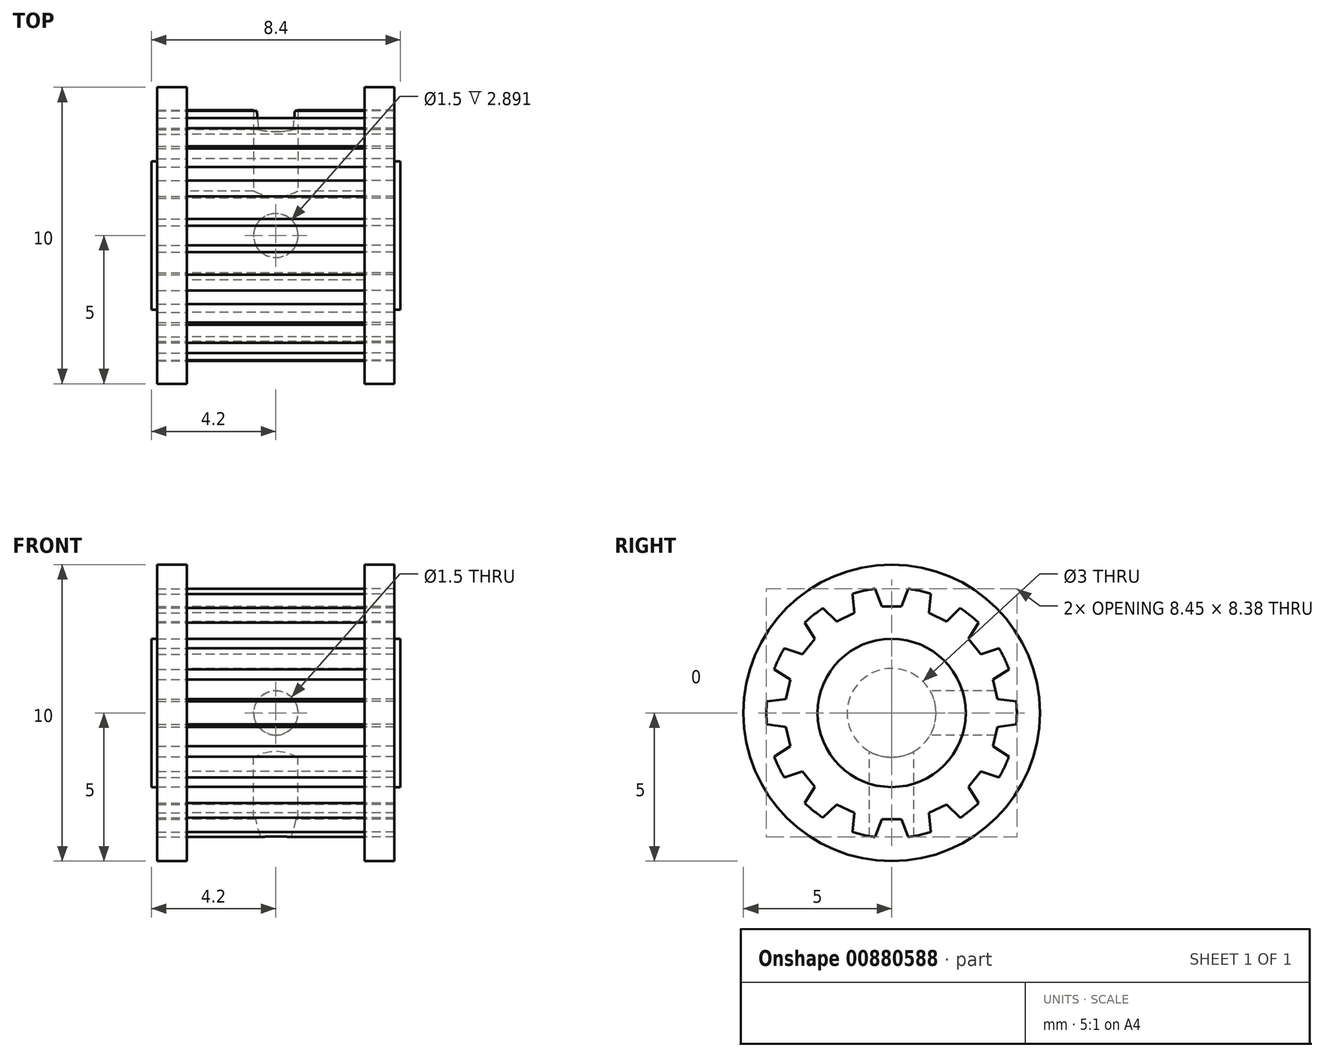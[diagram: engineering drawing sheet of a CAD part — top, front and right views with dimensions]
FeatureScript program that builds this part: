
annotation { "Feature Type Name" : "Feature", "Feature Type Description" : "" }
export const myFeature = defineFeature(function(context is Context, id is Id, definition is map)
    precondition{}
    {
        {
            var Q0;
            Q0=qCreatedBy(makeId("Right.planeOp"),FACE);
            var sketch = newSketch(context, id + "F0", { "sketchPlane" : qUnion([Q0])});
            skCircle(sketch, "E0", {"center": v(0, 0) * mm, "radius": 4.23 * mm});
            skSolve(sketch);
        }
        {
            var Q0;
            Q0=makeQuery(id+"F0.imprint","IMPRINT",FACE,{"disambiguationData":[TD([[makeQuery(id+"F0.imprint","IMPRINT",EDGE,{"derivedFrom":sQuery(id+"F0.wireOp",EDGE,"E0")}),1.0]])]});
            extrude(context, id + "F1", {"entities" : qUnion([Q0]), "endBound" : BoundingType.SYMMETRIC, "depth" : 6 * mm, "offsetDistance" : 25 * mm});
        }
        {
            var Q0;
            Q0=makeQuery(id+"F1.opExtrude","CAP_FACE",FACE,{"disambiguationData":[OSD([sQuery(id+"F0.wireOp",EDGE,"E0")])],"isStart":true});
            var sketch = newSketch(context, id + "F2", { "sketchPlane" : qUnion([Q0])});
            skCircle(sketch, "E1", {"center": v(0, 0) * mm, "radius": 1.5 * mm});
            skSolve(sketch);
        }
        {
            var Q0;
            Q0=makeQuery(id+"F2.imprint","IMPRINT",FACE,{"disambiguationData":[TD([[makeQuery(id+"F2.imprint","IMPRINT",EDGE,{"derivedFrom":sQuery(id+"F2.wireOp",EDGE,"E1")}),1.0]])]});
            extrude(context, id + "F3", {"entities" : qUnion([Q0]), "operationType" : NewBodyOperationType.REMOVE, "oppositeDirection" : true, "depth" : 6 * mm, "offsetDistance" : 25 * mm});
        }
        {
            var Q0;
            Q0=qCreatedBy(makeId("Front.planeOp"),FACE);
            var sketch = newSketch(context, id + "F4", { "sketchPlane" : qUnion([Q0])});
            skCircle(sketch, "E2", {"center": v(0, 0) * mm, "radius": 0.75 * mm});
            skSolve(sketch);
        }
        {
            var Q0;
            Q0=makeQuery(id+"F1.opExtrude","CAP_FACE",FACE,{"disambiguationData":[OSD([sQuery(id+"F0.wireOp",EDGE,"E0")])],"isStart":true});
            var sketch = newSketch(context, id + "F5", { "sketchPlane" : qUnion([Q0])});
            skLineSegment(sketch, "E3", {"start": v(0, 0) * mm, "end": v(0, 3.58) * mm});
            skLineSegment(sketch, "E4", {"start": v(0, 3.58) * mm, "end": v(0.34, 3.58) * mm});
            skLineSegment(sketch, "E5", {"start": v(0.33, 3.58) * mm, "end": v(0.59, 4.28) * mm});
            skLineSegment(sketch, "E6", {"start": v(0, 3.58) * mm, "end": v(0, 4.3) * mm});
            skLineSegment(sketch, "E7.MirrorCS", {"start": v(-0.33, 3.58) * mm, "end": v(-0.59, 4.28) * mm});
            skLineSegment(sketch, "E8.MirrorCS", {"start": v(0, 3.58) * mm, "end": v(-0.34, 3.58) * mm});
            skLineSegment(sketch, "E9", {"start": v(-0.59, 4.28) * mm, "end": v(0, 4.3) * mm});
            skLineSegment(sketch, "E10.MirrorCS", {"start": v(0.59, 4.28) * mm, "end": v(0, 4.3) * mm});
            skSolve(sketch);
        }
        {
            var Q0;
            {var subQ0=sQuery(id+"F5.wireOp",EDGE,"E4");Q0=makeQuery(id+"F5.imprint","IMPRINT",FACE,{"disambiguationData":[TD([[makeQuery(id+"F5.imprint","IMPRINT",EDGE,{"derivedFrom":subQ0}),1.0]])]});}
            var Q1;
            {var subQ0=sQuery(id+"F5.wireOp",EDGE,"E10.MirrorCS");Q1=makeQuery(id+"F5.imprint","IMPRINT",FACE,{"disambiguationData":[TD([[makeQuery(id+"F5.imprint","IMPRINT",EDGE,{"derivedFrom":subQ0}),1.0]])]});}
            var Q2;
            {var subQ0=sQuery(id+"F5.wireOp",EDGE,"E9");Q2=makeQuery(id+"F5.imprint","IMPRINT",FACE,{"disambiguationData":[TD([[makeQuery(id+"F5.imprint","IMPRINT",EDGE,{"derivedFrom":subQ0}),-1.0]])]});}
            var Q3;
            {var subQ0=sQuery(id+"F5.wireOp",EDGE,"E8.MirrorCS");Q3=makeQuery(id+"F5.imprint","IMPRINT",FACE,{"disambiguationData":[TD([[makeQuery(id+"F5.imprint","IMPRINT",EDGE,{"derivedFrom":subQ0}),-1.0]])]});}
            extrude(context, id + "F6", {"entities" : qUnion([Q0, Q1, Q2, Q3]), "operationType" : NewBodyOperationType.REMOVE, "oppositeDirection" : true, "depth" : 7 * mm, "offsetDistance" : 25 * mm});
        }
        {
            var Q0;
            Q0=makeQuery(id+"F6.boolean.opBoolean","COPY",FACE,{"derivedFrom":makeQuery(id+"F6.opExtrude","SWEPT_FACE",FACE,{"disambiguationData":[OSD([sQuery(id+"F5.wireOp",EDGE,"E7.MirrorCS")])]})});
            var Q1;
            Q1=makeQuery(id+"F6.boolean.opBoolean","COPY",FACE,{"derivedFrom":makeQuery(id+"F6.opExtrude","SWEPT_FACE",FACE,{"disambiguationData":[OSD([sQuery(id+"F5.wireOp",EDGE,"E4"),sQuery(id+"F5.wireOp",EDGE,"E8.MirrorCS")])]})});
            var Q2;
            Q2=makeQuery(id+"F6.boolean.opBoolean","COPY",FACE,{"derivedFrom":makeQuery(id+"F6.opExtrude","SWEPT_FACE",FACE,{"disambiguationData":[OSD([sQuery(id+"F5.wireOp",EDGE,"E5")])]})});
            var Q3;
            Q3=makeQuery(id+"F1.opExtrude","SWEPT_FACE",FACE,{"disambiguationData":[OSD([sQuery(id+"F0.wireOp",EDGE,"E0")])]});
            circularPattern(context, id + "F7", {"patternType" : PatternType.FACE, "faces" : qUnion([Q0, Q1, Q2]), "axis" : qUnion([Q3]), "angle" : 6.28 * radian, "instanceCount" : 14, "equalSpace" : true});
        }
        {
            var Q0;
            Q0=makeQuery(id+"F4.imprint","IMPRINT",FACE,{"disambiguationData":[TD([[makeQuery(id+"F4.imprint","IMPRINT",EDGE,{"derivedFrom":sQuery(id+"F4.wireOp",EDGE,"E2")}),1.0]])]});
            extrude(context, id + "F8", {"entities" : qUnion([Q0]), "operationType" : NewBodyOperationType.REMOVE, "oppositeDirection" : true, "depth" : 5 * mm, "offsetDistance" : 25 * mm});
        }
        {
            var Q0;
            Q0=qCreatedBy(makeId("Top.planeOp"),FACE);
            var sketch = newSketch(context, id + "F9", { "sketchPlane" : qUnion([Q0])});
            skCircle(sketch, "E11", {"center": v(0, 0) * mm, "radius": 0.75 * mm});
            skSolve(sketch);
        }
        {
            var Q0;
            Q0=makeQuery(id+"F9.imprint","IMPRINT",FACE,{"disambiguationData":[TD([[makeQuery(id+"F9.imprint","IMPRINT",EDGE,{"derivedFrom":sQuery(id+"F9.wireOp",EDGE,"E11")}),1.0]])]});
            extrude(context, id + "F10", {"entities" : qUnion([Q0]), "operationType" : NewBodyOperationType.REMOVE, "oppositeDirection" : true, "depth" : 5 * mm, "offsetDistance" : 25 * mm});
        }
        {
            var Q0;
            Q0=makeQuery(id+"F1.opExtrude","CAP_FACE",FACE,{"disambiguationData":[OSD([sQuery(id+"F0.wireOp",EDGE,"E0")])],"isStart":false});
            var sketch = newSketch(context, id + "F11", { "sketchPlane" : qUnion([Q0])});
            skCircle(sketch, "E12", {"center": v(0, 0) * mm, "radius": 5 * mm});
            skSolve(sketch);
        }
        {
            var Q0;
            Q0=makeQuery(id+"F11.imprint","IMPRINT",FACE,{"disambiguationData":[TD([[makeQuery(id+"F11.imprint","IMPRINT",EDGE,{"derivedFrom":sQuery(id+"F11.wireOp",EDGE,"E12")}),1.0]])]});
            var Q1;
            Q1=makeQuery(id+"F11.imprint","IMPRINT",FACE,{"disambiguationData":[TD([[makeQuery(id+"F11.imprint","IMPRINT",EDGE,{"derivedFrom":makeQuery(id+"F3.boolean.opBoolean","COPY",EDGE,{"derivedFrom":makeQuery(id+"F3.opExtrude","CAP_EDGE",EDGE,{"disambiguationData":[OSD([sQuery(id+"F2.wireOp",EDGE,"E1")])],"isStart":false})})}),1.0]])]});
            extrude(context, id + "F12", {"entities" : qUnion([Q0, Q1]), "operationType" : NewBodyOperationType.ADD, "depth" : 1 * mm, "offsetDistance" : 25 * mm});
        }
        {
            var Q0;
            Q0=makeQuery(id+"F1.opExtrude","CAP_FACE",FACE,{"disambiguationData":[OSD([sQuery(id+"F0.wireOp",EDGE,"E0")])],"isStart":true});
            var sketch = newSketch(context, id + "F13", { "sketchPlane" : qUnion([Q0])});
            skCircle(sketch, "E13", {"center": v(0, 0) * mm, "radius": 5 * mm});
            skSolve(sketch);
        }
        {
            var Q0;
            Q0=makeQuery(id+"F13.imprint","IMPRINT",FACE,{"disambiguationData":[TD([[makeQuery(id+"F13.imprint","IMPRINT",EDGE,{"derivedFrom":sQuery(id+"F13.wireOp",EDGE,"E13")}),1.0]])]});
            var Q1;
            Q1=makeQuery(id+"F13.imprint","IMPRINT",FACE,{"disambiguationData":[TD([[makeQuery(id+"F13.imprint","IMPRINT",EDGE,{"derivedFrom":makeQuery(id+"F3.boolean.opBoolean","COPY",EDGE,{"derivedFrom":makeQuery(id+"F3.opExtrude","CAP_EDGE",EDGE,{"disambiguationData":[OSD([sQuery(id+"F2.wireOp",EDGE,"E1")])],"isStart":true})})}),-1.0]])]});
            extrude(context, id + "F14", {"entities" : qUnion([Q0, Q1]), "operationType" : NewBodyOperationType.ADD, "depth" : 1 * mm, "offsetDistance" : 25 * mm});
        }
        {
            var Q0;
            Q0=makeQuery(id+"F12.opExtrude","CAP_FACE",FACE,{"disambiguationData":[OSD([sQuery(id+"F2.wireOp",EDGE,"E1"),sQuery(id+"F11.wireOp",EDGE,"E12")])],"isStart":false});
            var sketch = newSketch(context, id + "F15", { "sketchPlane" : qUnion([Q0])});
            skCircle(sketch, "E14", {"center": v(0, 0) * mm, "radius": 2.5 * mm});
            skSolve(sketch);
        }
        {
            var Q0;
            Q0=makeQuery(id+"F15.imprint","IMPRINT",FACE,{"disambiguationData":[TD([[makeQuery(id+"F15.imprint","IMPRINT",EDGE,{"derivedFrom":sQuery(id+"F15.wireOp",EDGE,"E14")}),1.0]])]});
            extrude(context, id + "F16", {"entities" : qUnion([Q0]), "operationType" : NewBodyOperationType.ADD, "depth" : .2 * mm, "offsetDistance" : 25 * mm});
        }
        {
            var Q0;
            Q0=makeQuery(id+"F14.opExtrude","CAP_FACE",FACE,{"disambiguationData":[OSD([sQuery(id+"F2.wireOp",EDGE,"E1"),sQuery(id+"F13.wireOp",EDGE,"E13")])],"isStart":false});
            var sketch = newSketch(context, id + "F17", { "sketchPlane" : qUnion([Q0])});
            skCircle(sketch, "E15", {"center": v(0, 0) * mm, "radius": 2.5 * mm});
            skSolve(sketch);
        }
        {
            var Q0;
            Q0=makeQuery(id+"F17.imprint","IMPRINT",FACE,{"disambiguationData":[TD([[makeQuery(id+"F17.imprint","IMPRINT",EDGE,{"derivedFrom":sQuery(id+"F17.wireOp",EDGE,"E15")}),1.0]])]});
            extrude(context, id + "F18", {"entities" : qUnion([Q0]), "operationType" : NewBodyOperationType.ADD, "depth" : .2 * mm, "offsetDistance" : 25 * mm});
        }
    });
